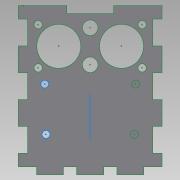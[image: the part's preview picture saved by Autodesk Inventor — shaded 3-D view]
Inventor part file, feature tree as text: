
AUTODESK INVENTOR PART (.ipt)
format: ipt  version: 2015 SP1 (Build 190203100, 203)  size: 236,544 bytes
history: native  units: mm
features: extrude x4, sketch x3, projected_geometry x1
ambient origin geometry x8: Origin, YZ Plane, XZ Plane, XY Plane, X Axis, Y Axis, Z Axis, Center Point
bodies: Body1 (feature_tree)
feature tree (8):
  extrude  "Extrusion2"  Depth=3.0mm
  extrude  "Extrusion3"  Depth=3.0mm
  sketch  "Sketch3"  dims[d14=180.0deg d15=3.0mm d17=7.675mm d18=7.675mm d21=3.0mm d22=0.0mm d23=2.999814mm d24=0.5mm d25=0.5mm d26=3.0mm d27=0.0mm d28=0.5mm d29=0.5mm d30=11.700171mm d31=11.699829mm d32=7.675mm d33=7.675mm d34=11.699829mm d35=11.700171mm d45=8.061mm d46=8.061mm d47=10.0mm d48=0.0mm d49=3.0mm d50=0.0mm]
  extrude  "Extrusion4"  Depth=3.0mm
  extrude  "Extrusion5"  Depth=3.0mm
  sketch  "Sketch1"  dims[d0=10.0mm d1=3.0mm]
  sketch  "Sketch2"  dims[d2=20.0mm d4=15.0mm d5=20.0mm d7=15.0mm d13=3.0mm]
  projected_geometry  "Projected Loop1"
